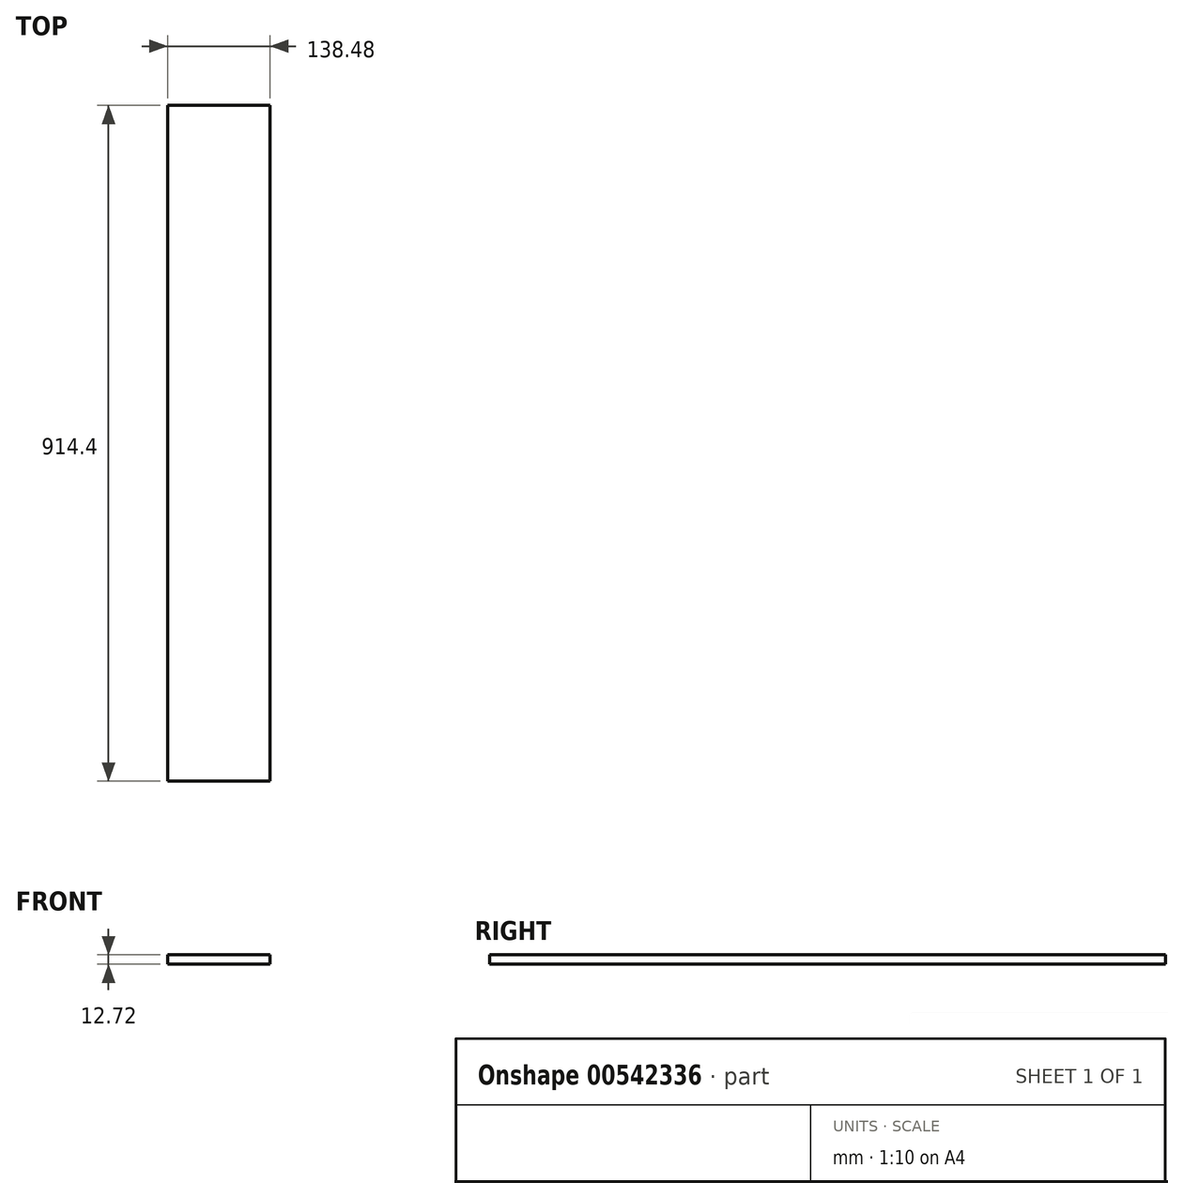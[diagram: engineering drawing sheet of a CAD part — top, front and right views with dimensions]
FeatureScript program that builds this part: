
annotation { "Feature Type Name" : "Feature", "Feature Type Description" : "" }
export const myFeature = defineFeature(function(context is Context, id is Id, definition is map)
    precondition{}
    {
        {
            var Q0;
            Q0=qCreatedBy(makeId("Front.planeOp"),FACE);
            var sketch = newSketch(context, id + "F0", { "sketchPlane" : qUnion([Q0])});
            skLineSegment(sketch, "E0.bottom", {"start": v(-69.24, -6.36) * mm, "end": v(69.24, -6.36) * mm});
            skLineSegment(sketch, "E0.top", {"start": v(-69.24, 6.36) * mm, "end": v(69.24, 6.36) * mm});
            skLineSegment(sketch, "E0.left", {"start": v(-69.24, -6.36) * mm, "end": v(-69.24, 6.36) * mm});
            skLineSegment(sketch, "E0.right", {"start": v(69.24, -6.36) * mm, "end": v(69.24, 6.36) * mm});
            skPoint(sketch, "E0.middle", {"position": v(0, 0) * mm});
            skSolve(sketch);
        }
        {
            var Q0;
            Q0=makeQuery(id+"F0.imprint","IMPRINT",FACE,{"disambiguationData":[TD([[makeQuery(id+"F0.imprint","IMPRINT",EDGE,{"derivedFrom":sQuery(id+"F0.wireOp",EDGE,"E0.bottom")}),1.0]])]});
            extrude(context, id + "F1", {"entities" : qUnion([Q0]), "depth" : 914.4 * mm, "offsetDistance" : 25.4 * mm});
        }
    });
